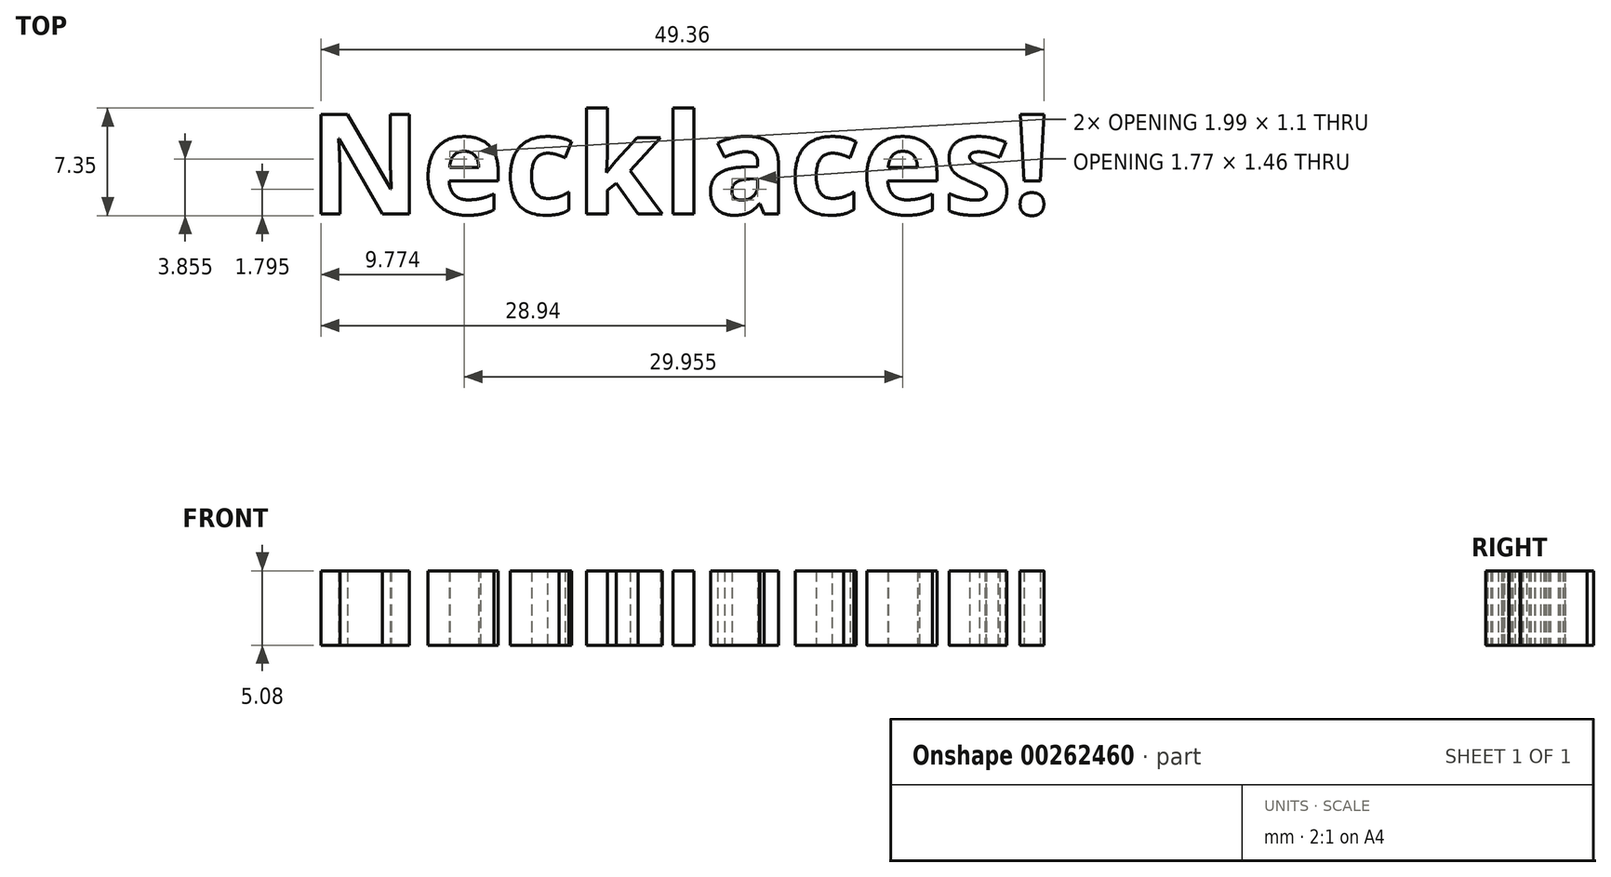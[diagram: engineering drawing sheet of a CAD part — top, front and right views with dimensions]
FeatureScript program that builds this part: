
annotation { "Feature Type Name" : "Feature", "Feature Type Description" : "" }
export const myFeature = defineFeature(function(context is Context, id is Id, definition is map)
    precondition{}
    {
        {
            var Q0;
            Q0=qCreatedBy(makeId("Top.planeOp"),FACE);
            var sketch = newSketch(context, id + "F0", { "sketchPlane" : qUnion([Q0])});
            skText(sketch, "E0", { "text": "Necklaces!", "fontName": "OpenSans-Bold.ttf"});
            const initialGuessF0  = {"E0": [-0.02623, -0.00285, 1, 0, 0.00685]};
            skSetInitialGuess(sketch, initialGuessF0);
            skSolve(sketch);
        }
        {
            var Q0;
            Q0 = qSketchRegion(id + "F0", true);
            extrude(context, id + "F1", {"entities" : qUnion([Q0]), "depth" : 5.08 * mm});
        }
    });
